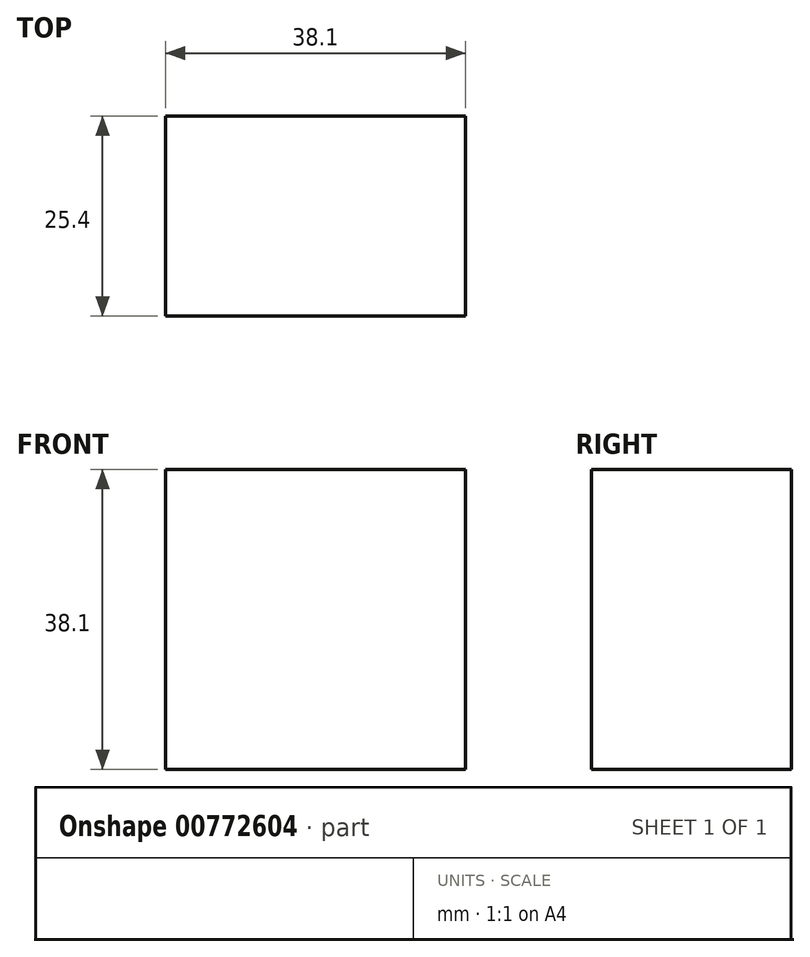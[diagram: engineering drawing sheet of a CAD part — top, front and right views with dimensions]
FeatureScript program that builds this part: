
annotation { "Feature Type Name" : "Feature", "Feature Type Description" : "" }
export const myFeature = defineFeature(function(context is Context, id is Id, definition is map)
    precondition{}
    {
        {
            var Q0;
            Q0=qCreatedBy(makeId("Front.planeOp"),FACE);
            var sketch = newSketch(context, id + "F0", { "sketchPlane" : qUnion([Q0])});
            skLineSegment(sketch, "E0", {"start": v(0, 0) * mm, "end": v(38.1, 0) * mm});
            skLineSegment(sketch, "E1", {"start": v(38.1, 0) * mm, "end": v(38.1, 38.1) * mm});
            skLineSegment(sketch, "E2", {"start": v(38.1, 38.1) * mm, "end": v(0, 38.1) * mm});
            skLineSegment(sketch, "E3", {"start": v(0, 38.1) * mm, "end": v(0, 0) * mm});
            skSolve(sketch);
        }
        {
            var Q0;
            Q0=makeQuery(id+"F0.imprint","IMPRINT",FACE,{"disambiguationData":[TD([[makeQuery(id+"F0.imprint","IMPRINT",EDGE,{"derivedFrom":sQuery(id+"F0.wireOp",EDGE,"E0")}),1.0]])]});
            extrude(context, id + "F1", {"entities" : qUnion([Q0]), "depth" : 25.4 * mm, "offsetDistance" : 25.4 * mm});
        }
    });
